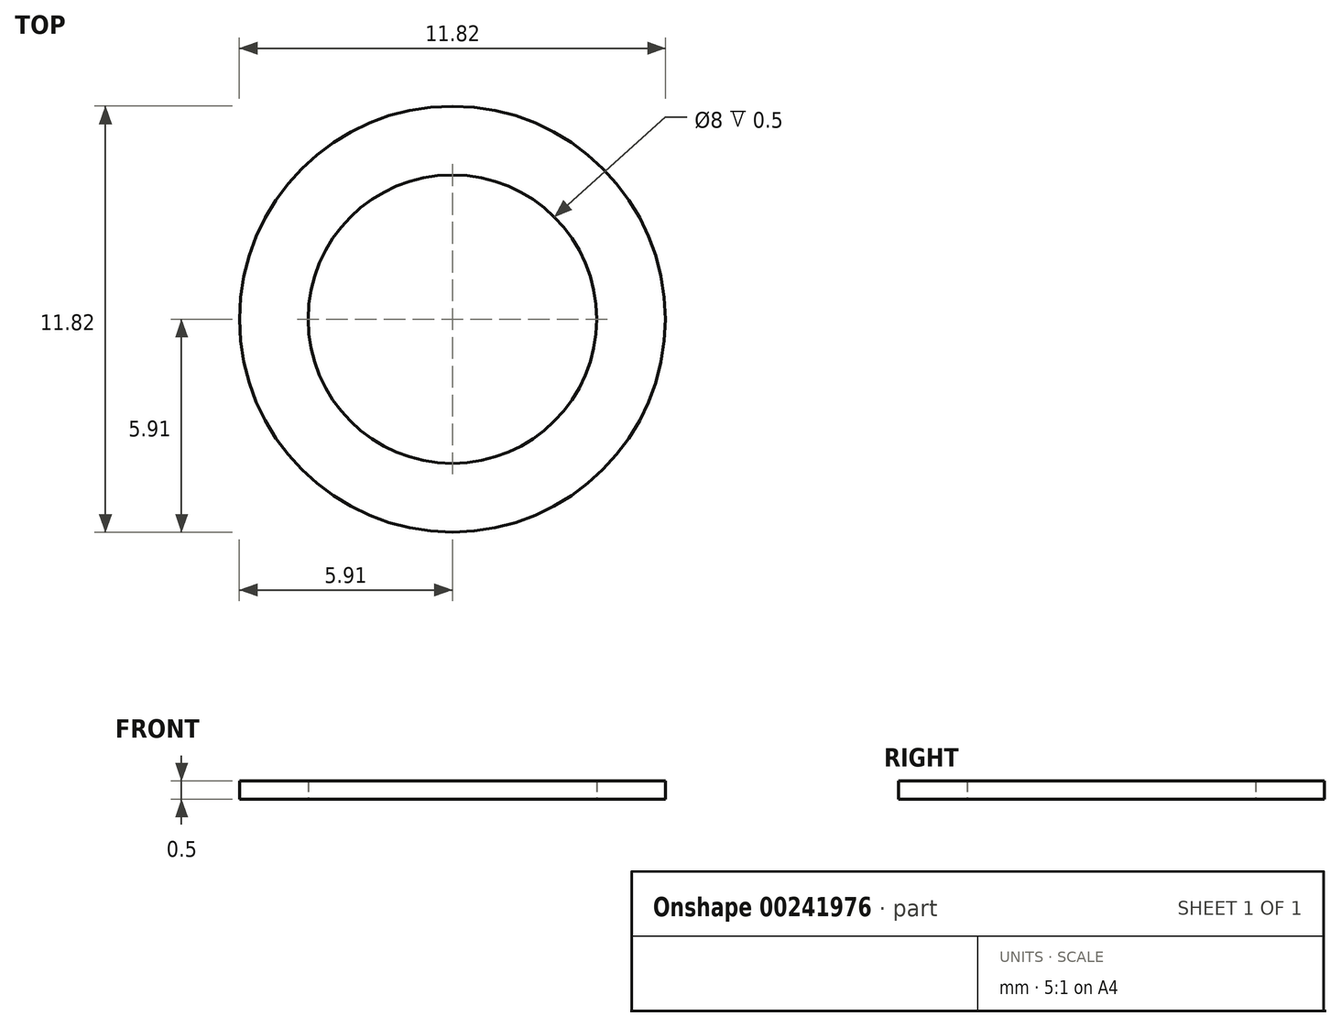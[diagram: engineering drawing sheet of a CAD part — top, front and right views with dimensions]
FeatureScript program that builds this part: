
annotation { "Feature Type Name" : "Feature", "Feature Type Description" : "" }
export const myFeature = defineFeature(function(context is Context, id is Id, definition is map)
    precondition{}
    {
        {
            var Q0;
            Q0=qCreatedBy(makeId("Top.planeOp"),FACE);
            var sketch = newSketch(context, id + "F0", { "sketchPlane" : qUnion([Q0])});
            skCircle(sketch, "E0", {"center": v(0, 0) * mm, "radius": 5.9 * mm});
            skCircle(sketch, "E1", {"center": v(0, 0) * mm, "radius": 4 * mm});
            skSolve(sketch);
        }
        {
            var Q0;
            Q0=makeQuery(id+"F0.imprint","IMPRINT",FACE,{"disambiguationData":[TD([[makeQuery(id+"F0.imprint","IMPRINT",EDGE,{"derivedFrom":sQuery(id+"F0.wireOp",EDGE,"E0")}),1.0]])]});
            extrude(context, id + "F1", {"entities" : qUnion([Q0]), "depth" : 0.5 * mm});
        }
    });
